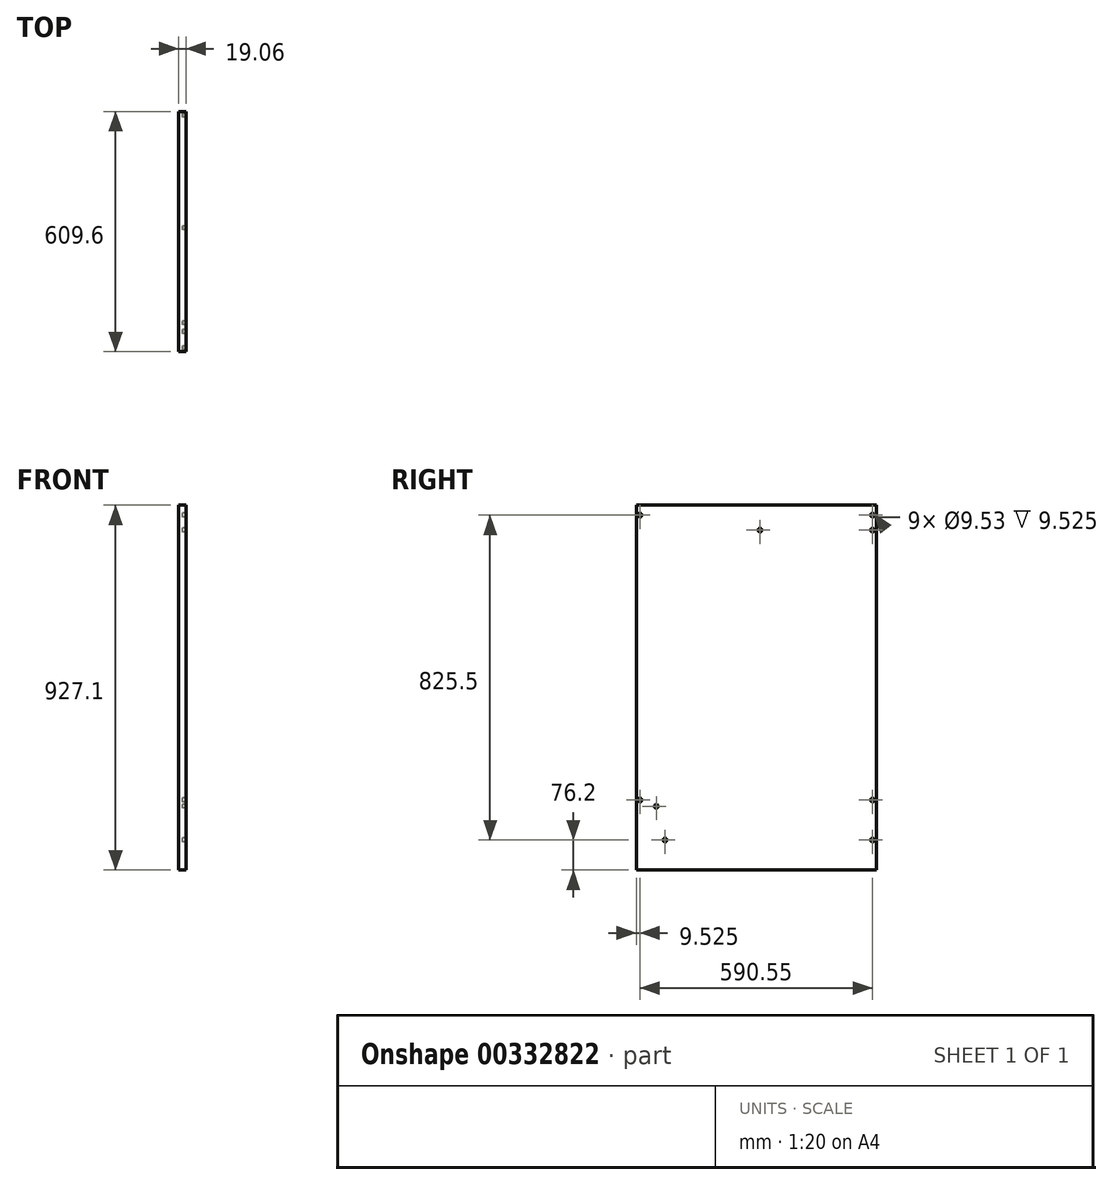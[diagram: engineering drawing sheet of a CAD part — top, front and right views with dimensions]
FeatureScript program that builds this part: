
annotation { "Feature Type Name" : "Feature", "Feature Type Description" : "" }
export const myFeature = defineFeature(function(context is Context, id is Id, definition is map)
    precondition{}
    {
        {
            var Q0;
            Q0=qCreatedBy(makeId("Right.planeOp"),FACE);
            var sketch = newSketch(context, id + "F0", { "sketchPlane" : qUnion([Q0])});
            skLineSegment(sketch, "E0.bottom", {"start": v(0, 0) * mm, "end": v(-609.6, 0) * mm});
            skLineSegment(sketch, "E0.top", {"start": v(0, 927.1) * mm, "end": v(-609.6, 927.1) * mm});
            skLineSegment(sketch, "E0.left", {"start": v(0, 0) * mm, "end": v(0, 927.1) * mm});
            skLineSegment(sketch, "E0.right", {"start": v(-609.6, 0) * mm, "end": v(-609.6, 927.1) * mm});
            skSolve(sketch);
        }
        {
            var Q0;
            Q0=qSketchRegion(id+"F0",true);
            extrude(context, id + "F1", {"entities" : qUnion([Q0]), "endBound" : BoundingType.SYMMETRIC, "depth" : 19.05 * mm});
        }
        {
            var Q0;
            Q0=qCreatedBy(makeId("Right.planeOp"),FACE);
            var sketch = newSketch(context, id + "F2", { "sketchPlane" : qUnion([Q0])});
            skCircle(sketch, "E1", {"center": v(-536.58, 63.5) * mm, "radius": 4.76 * mm, "construction": true});
            skCircle(sketch, "E2", {"center": v(-9.52, 76.2) * mm, "radius": 4.76 * mm});
            skCircle(sketch, "E3", {"center": v(-536.58, 177.8) * mm, "radius": 4.76 * mm, "construction": true});
            skCircle(sketch, "E4", {"center": v(-600.08, 177.8) * mm, "radius": 4.76 * mm});
            skCircle(sketch, "E5", {"center": v(-600.07, 901.7) * mm, "radius": 4.76 * mm});
            skCircle(sketch, "E6", {"center": v(-295.28, 1365.25) * mm, "radius": 4.76 * mm});
            skCircle(sketch, "E7", {"center": v(-295.28, 2089.15) * mm, "radius": 4.76 * mm});
            skCircle(sketch, "E8", {"center": v(-295.27, 863.6) * mm, "radius": 4.76 * mm});
            skCircle(sketch, "E9", {"center": v(-9.52, 863.6) * mm, "radius": 4.76 * mm});
            skCircle(sketch, "E10", {"center": v(-9.53, 2089.15) * mm, "radius": 4.76 * mm});
            skCircle(sketch, "E11", {"center": v(-9.53, 1365.25) * mm, "radius": 4.76 * mm});
            skCircle(sketch, "E12", {"center": v(-9.53, 901.7) * mm, "radius": 4.76 * mm});
            skCircle(sketch, "E13", {"center": v(-9.53, 177.8) * mm, "radius": 4.76 * mm});
            skCircle(sketch, "E14", {"center": v(-558.8, 161.92) * mm, "radius": 4.76 * mm});
            skCircle(sketch, "E15", {"center": v(-536.58, 76.2) * mm, "radius": 4.76 * mm});
            skLineSegment(sketch, "E16", {"start": v(-600.08, 152.4) * mm, "end": v(-499.65, 152.4) * mm, "construction": true});
            skSolve(sketch);
        }
        {
            var Q0;
            Q0=qSketchRegion(id+"F2",true);
            extrude(context, id + "F3", {"entities" : qUnion([Q0]), "operationType" : NewBodyOperationType.REMOVE, "depth" : 34.92 * mm});
        }
    });
